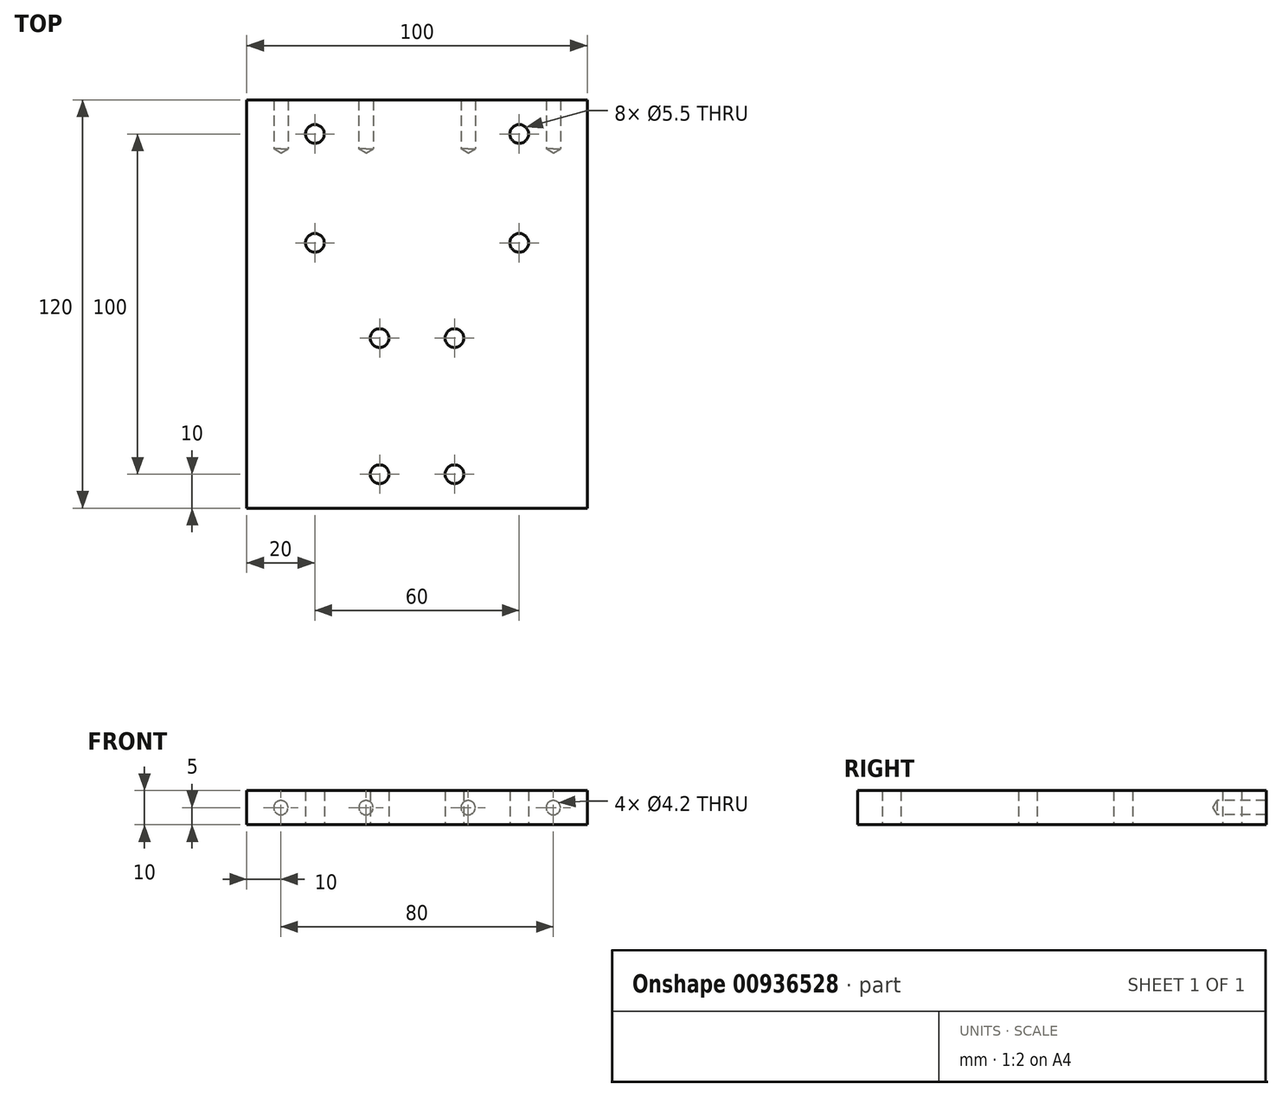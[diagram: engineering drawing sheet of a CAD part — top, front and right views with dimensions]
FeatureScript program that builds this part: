
annotation { "Feature Type Name" : "Feature", "Feature Type Description" : "" }
export const myFeature = defineFeature(function(context is Context, id is Id, definition is map)
    precondition{}
    {
        {
            var Q0;
            Q0=qCreatedBy(makeId("Right.planeOp"),FACE);
            var sketch = newSketch(context, id + "F0", { "sketchPlane" : qUnion([Q0])});
            skLineSegment(sketch, "E0", {"start": v(0, 0) * mm, "end": v(-120, 0) * mm});
            skLineSegment(sketch, "E1", {"start": v(-120, 0) * mm, "end": v(-120, 10) * mm});
            skLineSegment(sketch, "E2", {"start": v(-120, 10) * mm, "end": v(-10, 10) * mm});
            skLineSegment(sketch, "E3", {"start": v(-10, 10) * mm, "end": v(0, 10) * mm});
            skLineSegment(sketch, "E4", {"start": v(0, 10) * mm, "end": v(0, 0) * mm});
            skSolve(sketch);
        }
        {
            var Q0;
            Q0=makeQuery(id+"F0.imprint","IMPRINT",FACE,{"disambiguationData":[TD([[makeQuery(id+"F0.imprint","IMPRINT",EDGE,{"derivedFrom":sQuery(id+"F0.wireOp",EDGE,"E0")}),-1.0]])]});
            extrude(context, id + "F1", {"entities" : qUnion([Q0]), "depth" : 100 * mm, "offsetDistance" : 25 * mm});
        }
        {
            var Q0;
            Q0=makeQuery(id+"F1.opExtrude","SWEPT_FACE",FACE,{"disambiguationData":[OSD([sQuery(id+"F0.wireOp",EDGE,"E2")])]});
            var sketch = newSketch(context, id + "F2", { "sketchPlane" : qUnion([Q0])});
            skLineSegment(sketch, "E5", {"start": v(50, -120) * mm, "end": v(50, -120) * mm});
            skPoint(sketch, "E6", {"position": v(80, -42) * mm});
            skPoint(sketch, "E7", {"position": v(80, -10) * mm});
            skPoint(sketch, "E8", {"position": v(61, -70) * mm});
            skPoint(sketch, "E9", {"position": v(61, -110) * mm});
            skPoint(sketch, "E10.MirrorP", {"position": v(20, -10) * mm});
            skPoint(sketch, "E11.MirrorP", {"position": v(20, -42) * mm});
            skPoint(sketch, "E12.MirrorP", {"position": v(39, -70) * mm});
            skPoint(sketch, "E13.MirrorP", {"position": v(39, -110) * mm});
            skSolve(sketch);
        }
        {
            var Q0;
            Q0=sQuery(id+"F2.wireOp",VERTEX,"E7");
            var Q1;
            Q1=sQuery(id+"F2.wireOp",VERTEX,"E6");
            var Q2;
            Q2=sQuery(id+"F2.wireOp",VERTEX,"E11.MirrorP");
            var Q3;
            Q3=sQuery(id+"F2.wireOp",VERTEX,"E10.MirrorP");
            var Q4;
            Q4=sQuery(id+"F2.wireOp",VERTEX,"E12.MirrorP");
            var Q5;
            Q5=sQuery(id+"F2.wireOp",VERTEX,"E8");
            var Q6;
            Q6=sQuery(id+"F2.wireOp",VERTEX,"E9");
            var Q7;
            Q7=sQuery(id+"F2.wireOp",VERTEX,"E13.MirrorP");
            var Q8;
            Q8=makeQuery(id+"F1.opExtrude","SWEPT_BODY",BODY,{"disambiguationData":[OSD([sQuery(id+"F0.wireOp",EDGE,"E0"),sQuery(id+"F0.wireOp",EDGE,"E1"),sQuery(id+"F0.wireOp",EDGE,"E2"),sQuery(id+"F0.wireOp",EDGE,"lyHlLjzJ-6deT-chsd-zTzQ-zQpCOPTe06y6"),sQuery(id+"F0.wireOp",EDGE,"AcCQSEZg-wdSZ-OSCu-jus7-tjgHklufhvsH"),sQuery(id+"F0.wireOp",EDGE,"M2RyFoCD-YyVU-k2vH-ExBb-F0KgWRvY89yP")])]});
            hole(context, id + "F3", {"style" : HoleStyle.SIMPLE, "endStyle" : HoleEndStyle.THROUGH, "standardTappedOrClearance" : lookupTablePath({ "fit" : "Normal", "standard" : "ISO", "size" : "M5", "type" : "Clearance" }), "standardBlindInLast" : lookupTablePath({ "fit" : "Normal", "standard" : "ISO", "engagement" : "75%", "pitch" : "0.8 mm", "size" : "M5", "type" : "Clearance & tapped" }), "holeDiameter" : 5.5 * mm, "majorDiameter" : 6 * mm, "tappedDepth" : 12 * mm, "tapClearance" : 3, "locations" : qUnion([Q0, Q1, Q2, Q3, Q4, Q5, Q6, Q7]), "scope" : qUnion([Q8]), "startStyle" : HoleStartStyle.PART});
        }
        {
            var Q0;
            Q0=makeQuery(id+"F1.opExtrude","SWEPT_FACE",FACE,{"disambiguationData":[OSD([sQuery(id+"F0.wireOp",EDGE,"E4")])]});
            var sketch = newSketch(context, id + "F4", { "sketchPlane" : qUnion([Q0])});
            skLineSegment(sketch, "E14", {"start": v(-100, 5) * mm, "end": v(0, 5) * mm, "construction": true});
            skPoint(sketch, "E15", {"position": v(-90, 5) * mm});
            skPoint(sketch, "E16", {"position": v(-65, 5) * mm});
            skPoint(sketch, "E17", {"position": v(-35, 5) * mm});
            skPoint(sketch, "E18", {"position": v(-10, 5) * mm});
            skSolve(sketch);
        }
        {
            var Q0;
            Q0=sQuery(id+"F4.wireOp",VERTEX,"E15");
            var Q1;
            Q1=sQuery(id+"F4.wireOp",VERTEX,"E16");
            var Q2;
            Q2=sQuery(id+"F4.wireOp",VERTEX,"E17");
            var Q3;
            Q3=sQuery(id+"F4.wireOp",VERTEX,"E18");
            var Q4;
            Q4=makeQuery(id+"F1.opExtrude","SWEPT_BODY",BODY,{"disambiguationData":[OSD([sQuery(id+"F0.wireOp",EDGE,"E0"),sQuery(id+"F0.wireOp",EDGE,"E1"),sQuery(id+"F0.wireOp",EDGE,"E2"),sQuery(id+"F0.wireOp",EDGE,"E3"),sQuery(id+"F0.wireOp",EDGE,"E4")])]});
            hole(context, id + "F5", {"style" : HoleStyle.SIMPLE, "endStyle" : HoleEndStyle.BLIND, "standardTappedOrClearance" : lookupTablePath({ "standard" : "ISO", "engagement" : "75%", "pitch" : "0.8 mm", "size" : "M5", "type" : "Tapped" }), "standardBlindInLast" : lookupTablePath({ "standard" : "ISO", "fit" : "Normal", "engagement" : "75%", "pitch" : "0.8 mm", "size" : "M5", "type" : "Clearance & tapped" }), "holeDiameter" : 4.2 * mm, "majorDiameter" : 5 * mm, "showTappedDepth" : true, "holeDepth" : 14.4 * mm, "tappedDepth" : 12 * mm, "tapClearance" : 3, "locations" : qUnion([Q0, Q1, Q2, Q3]), "scope" : qUnion([Q4]), "startStyle" : HoleStartStyle.PART});
        }
    });
